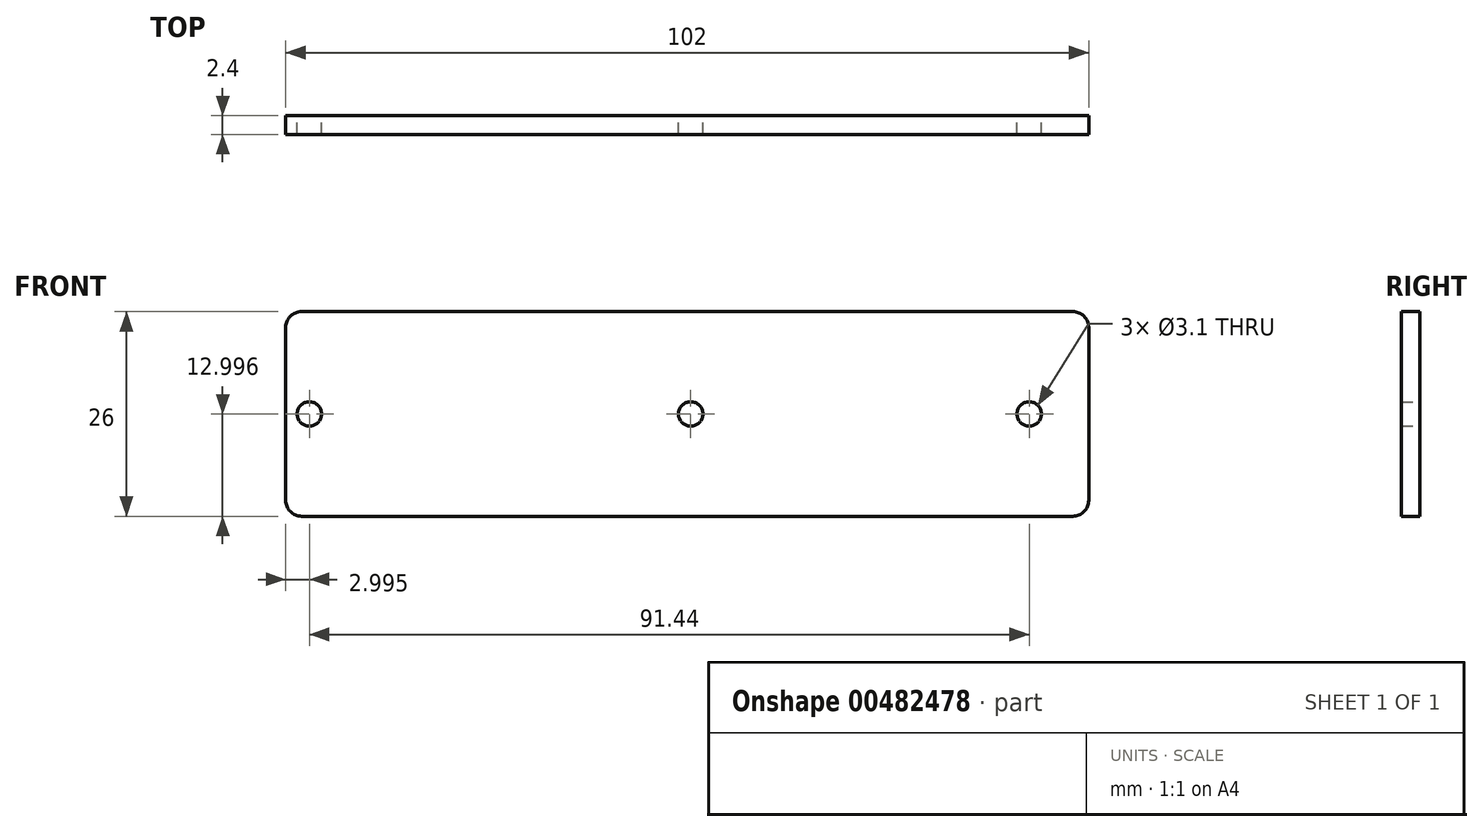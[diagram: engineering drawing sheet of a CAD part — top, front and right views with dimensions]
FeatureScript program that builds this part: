
annotation { "Feature Type Name" : "Feature", "Feature Type Description" : "" }
export const myFeature = defineFeature(function(context is Context, id is Id, definition is map)
    precondition{}
    {
        {
            var Q0;
            Q0=qCreatedBy(makeId("Front.planeOp"),FACE);
            var sketch = newSketch(context, id + "F0", { "sketchPlane" : qUnion([Q0])});
            skLineSegment(sketch, "E0.bottom", {"start": v(-48.1, 37.2) * mm, "end": v(49.9, 37.2) * mm});
            skLineSegment(sketch, "E0.top", {"start": v(-48.1, 11.2) * mm, "end": v(49.9, 11.2) * mm});
            skLineSegment(sketch, "E0.left", {"start": v(-50.1, 35.2) * mm, "end": v(-50.1, 13.2) * mm});
            skCircle(sketch, "E1", {"center": v(-47.1, 24.2) * mm, "radius": 1.55 * mm});
            skCircle(sketch, "E2", {"center": v(1.34, 24.2) * mm, "radius": 1.55 * mm});
            skCircle(sketch, "E3", {"center": v(44.34, 24.2) * mm, "radius": 1.55 * mm});
            skPoint(sketch, "E4.visualSharp", {"position": v(-50.1, 37.2) * mm});
            skArc(sketch, "E4.filletArc", {"start": v(-48.1, 37.2) * mm, "mid": v(-49.52, 36.62) * mm, "end": v(-50.1, 35.2) * mm});
            skPoint(sketch, "E5.visualSharp", {"position": v(-50.1, 11.2) * mm});
            skArc(sketch, "E5.filletArc", {"start": v(-50.1, 13.2) * mm, "mid": v(-49.52, 11.8) * mm, "end": v(-48.1, 11.2) * mm});
            skPoint(sketch, "E6.visualSharp", {"position": v(53.9, 37.2) * mm});
            skPoint(sketch, "E7.visualSharp", {"position": v(53.9, 11.2) * mm});
            skLineSegment(sketch, "E8", {"start": v(51.9, 35.2) * mm, "end": v(51.9, 13.2) * mm});
            skPoint(sketch, "E9.visualSharp", {"position": v(51.9, 37.2) * mm});
            skArc(sketch, "E9.filletArc", {"start": v(51.9, 35.2) * mm, "mid": v(51.3, 36.62) * mm, "end": v(49.9, 37.2) * mm});
            skPoint(sketch, "E10.visualSharp", {"position": v(51.9, 11.2) * mm});
            skArc(sketch, "E10.filletArc", {"start": v(49.9, 11.2) * mm, "mid": v(51.3, 11.8) * mm, "end": v(51.9, 13.2) * mm});
            skSolve(sketch);
        }
        {
            var Q0;
            Q0 = qSketchRegion(id + "F0", true);
            extrude(context, id + "F1", {"entities" : qUnion([Q0]), "depth" : 2.4 * mm, "offsetDistance" : 25 * mm});
        }
    });
